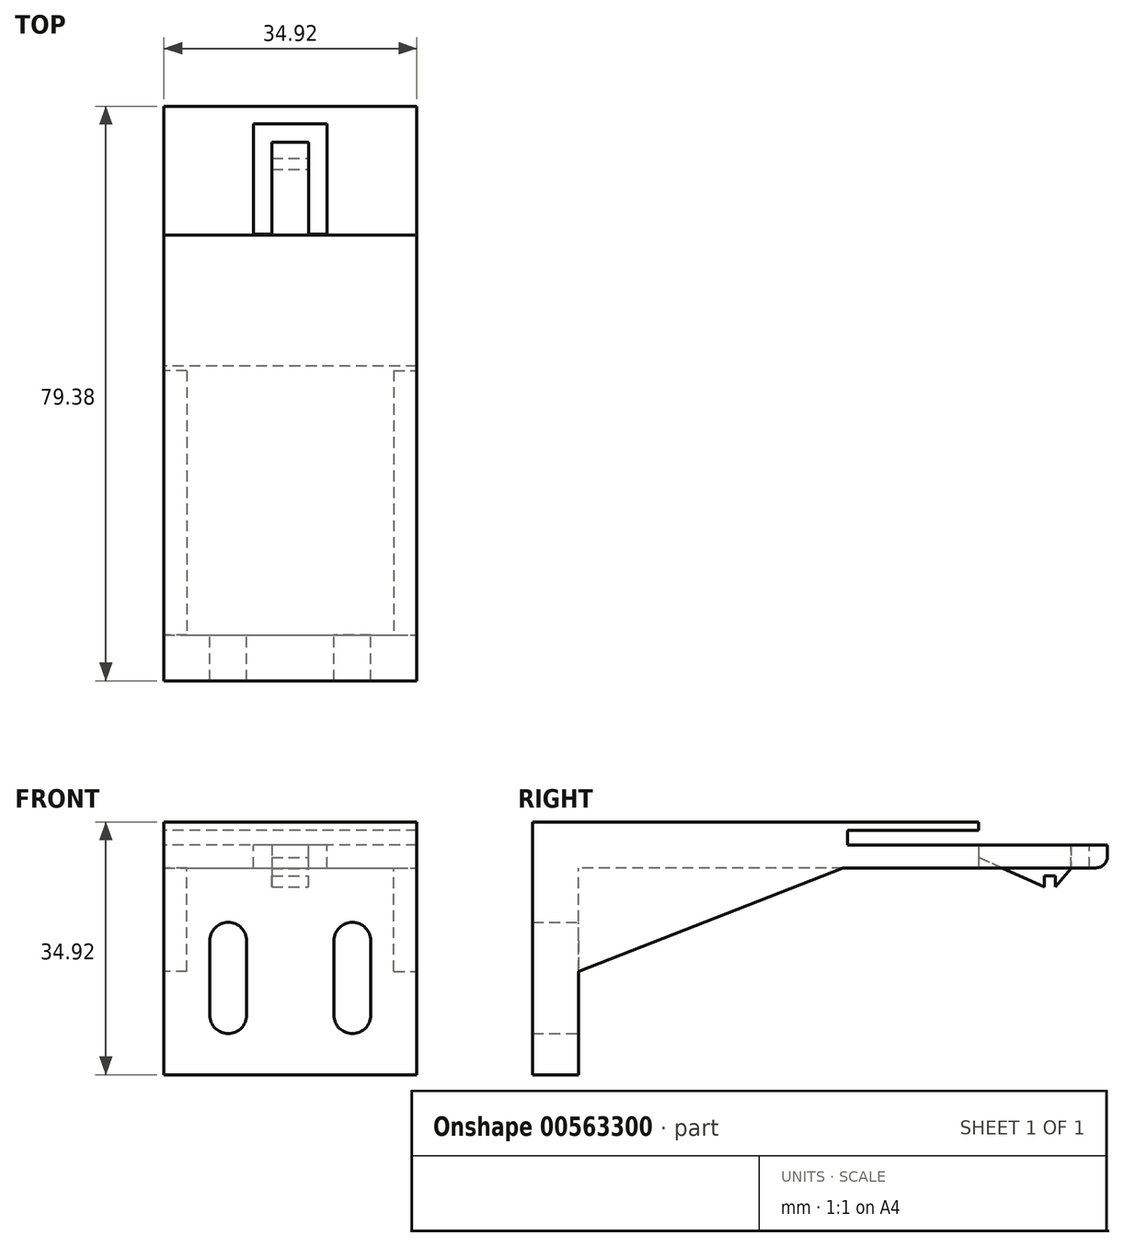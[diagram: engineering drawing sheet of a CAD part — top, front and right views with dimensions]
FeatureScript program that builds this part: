
annotation { "Feature Type Name" : "Feature", "Feature Type Description" : "" }
export const myFeature = defineFeature(function(context is Context, id is Id, definition is map)
    precondition{}
    {
        {
            var Q0;
            Q0=qCreatedBy(makeId("Front.planeOp"),FACE);
            var sketch = newSketch(context, id + "F0", { "sketchPlane" : qUnion([Q0])});
            skLineSegment(sketch, "E0.top", {"start": v(0, 34.93) * mm, "end": v(-34.93, 34.93) * mm});
            skLineSegment(sketch, "E0.left", {"start": v(0, 0) * mm, "end": v(0, 34.93) * mm});
            skLineSegment(sketch, "E0.right", {"start": v(-34.93, 0) * mm, "end": v(-34.93, 34.92) * mm});
            skLineSegment(sketch, "E1", {"start": v(-34.93, 0) * mm, "end": v(0, 0) * mm});
            skLineSegment(sketch, "E2", {"start": v(-28.57, 11.27) * mm, "end": v(-28.57, 5.29) * mm});
            skPoint(sketch, "E3.trimOffspring.end.orphan", {"position": v(-24.77, 14.54) * mm});
            skPoint(sketch, "E4.start.orphan", {"position": v(-24.77, 2.11) * mm});
            skLineSegment(sketch, "E5", {"start": v(-17.46, 0) * mm, "end": v(-17.46, 34.93) * mm});
            skLineSegment(sketch, "E6", {"start": v(-24.77, 14.54) * mm, "end": v(-24.77, 14.7) * mm});
            skArc(sketch, "E7", {"start": v(-6.35, 18.52) * mm, "mid": v(-8.9, 21.06) * mm, "end": v(-11.43, 18.52) * mm});
            skArc(sketch, "E8", {"start": v(-11.43, 8.21) * mm, "mid": v(-8.89, 5.67) * mm, "end": v(-6.35, 8.21) * mm});
            skLineSegment(sketch, "E9", {"start": v(-6.35, 18.52) * mm, "end": v(-6.35, 8.21) * mm});
            skLineSegment(sketch, "E10", {"start": v(-11.43, 18.52) * mm, "end": v(-11.43, 8.21) * mm});
            skPoint(sketch, "E11.start.orphan", {"position": v(-8.89, 2.11) * mm});
            skPoint(sketch, "E12.trimOffspring.end.orphan", {"position": v(-8.9, 34.93) * mm});
            skArc(sketch, "E13.MirrorCS", {"start": v(-23.5, 8.21) * mm, "mid": v(-26.04, 5.67) * mm, "end": v(-28.58, 8.21) * mm});
            skLineSegment(sketch, "E14.MirrorCS", {"start": v(-23.5, 18.52) * mm, "end": v(-23.5, 8.21) * mm});
            skLineSegment(sketch, "E15.MirrorCS", {"start": v(-28.58, 18.52) * mm, "end": v(-28.58, 8.21) * mm});
            skArc(sketch, "E16.MirrorCS", {"start": v(-28.58, 18.52) * mm, "mid": v(-26.04, 21.06) * mm, "end": v(-23.5, 18.52) * mm});
            skSolve(sketch);
        }
        {
            var Q0;
            Q0 = qSketchRegion(id + "F0", true);
            extrude(context, id + "F1", {"entities" : qUnion([Q0]), "depth" : 6.35 * mm, "offsetDistance" : 25.4 * mm});
        }
        {
            var Q0;
            Q0=makeQuery(id+"F1.opExtrude","CAP_FACE",FACE,{"disambiguationData":[OSD([sQuery(id+"F0.wireOp",EDGE,"E0.top"),sQuery(id+"F0.wireOp",EDGE,"E0.left"),sQuery(id+"F0.wireOp",EDGE,"E0.right"),sQuery(id+"F0.wireOp",EDGE,"E1"),sQuery(id+"F0.wireOp",EDGE,"E2"),sQuery(id+"F0.wireOp",EDGE,"H6N8bAam-MXU0-CgfR-VFbv-wHTDPL8jopEp"),sQuery(id+"F0.wireOp",EDGE,"061fb9ac-4066-484d-a823-505c24cabc42.trimOffspring"),sQuery(id+"F0.wireOp",EDGE,"351367ec-2027-426c-9255-262ef1abbde6.trimOffspring"),sQuery(id+"F0.wireOp",EDGE,"85143ae7-1432-489c-9ee5-68bd793780470.MirrorCS"),sQuery(id+"F0.wireOp",EDGE,"85143ae7-1432-489c-9ee5-68bd793780471.MirrorCS"),sQuery(id+"F0.wireOp",EDGE,"85143ae7-1432-489c-9ee5-68bd793780472.MirrorCS"),sQuery(id+"F0.wireOp",EDGE,"85143ae7-1432-489c-9ee5-68bd793780473.MirrorCS")])],"isStart":true});
            var sketch = newSketch(context, id + "F2", { "sketchPlane" : qUnion([Q0])});
            skLineSegment(sketch, "E17.bottom", {"start": v(34.93, 34.93) * mm, "end": v(0, 34.93) * mm});
            skLineSegment(sketch, "E17.top", {"start": v(34.93, 28.57) * mm, "end": v(0, 28.57) * mm});
            skLineSegment(sketch, "E17.left", {"start": v(34.93, 34.93) * mm, "end": v(34.93, 28.57) * mm});
            skLineSegment(sketch, "E17.right", {"start": v(0, 34.93) * mm, "end": v(0, 28.57) * mm});
            skSolve(sketch);
        }
        {
            var Q0;
            Q0=makeQuery(id+"F2.imprint","IMPRINT",FACE,{"disambiguationData":[TD([[makeQuery(id+"F2.imprint","IMPRINT",EDGE,{"derivedFrom":sQuery(id+"F2.wireOp",EDGE,"E17.bottom")}),-1.0]])]});
            extrude(context, id + "F3", {"entities" : qUnion([Q0]), "operationType" : NewBodyOperationType.ADD, "depth" : 73.02 * mm, "offsetDistance" : 25.4 * mm});
        }
        {
            var Q0;
            Q0=makeQuery(id+"F3.boolean.opBoolean","MERGE",FACE,{"derivedFrom":[makeQuery(id+"F1.opExtrude","SWEPT_FACE",FACE,{"disambiguationData":[OSD([sQuery(id+"F0.wireOp",EDGE,"E0.left")])]}),makeQuery(id+"F3.opExtrude","SWEPT_FACE",FACE,{"disambiguationData":[OSD([sQuery(id+"F2.wireOp",EDGE,"E17.right")])]})]});
            var sketch = newSketch(context, id + "F4", { "sketchPlane" : qUnion([Q0])});
            skLineSegment(sketch, "E18", {"start": v(0, 14.29) * mm, "end": v(36.51, 28.57) * mm});
            skLineSegment(sketch, "E19", {"start": v(36.51, 28.57) * mm, "end": v(0, 28.57) * mm});
            skLineSegment(sketch, "E20", {"start": v(0, 28.57) * mm, "end": v(0, 14.29) * mm});
            skSolve(sketch);
        }
        {
            var Q0;
            Q0=makeQuery(id+"F4.imprint","IMPRINT",FACE,{"disambiguationData":[TD([[makeQuery(id+"F4.imprint","IMPRINT",EDGE,{"derivedFrom":sQuery(id+"F4.wireOp",EDGE,"E18")}),1.0]])]});
            extrude(context, id + "F5", {"entities" : qUnion([Q0]), "operationType" : NewBodyOperationType.ADD, "oppositeDirection" : true, "depth" : 3.17 * mm, "offsetDistance" : 25.4 * mm});
        }
        {
            var Q0;
            Q0=makeQuery(id+"F3.boolean.opBoolean","MERGE",FACE,{"derivedFrom":[makeQuery(id+"F1.opExtrude","SWEPT_FACE",FACE,{"disambiguationData":[OSD([sQuery(id+"F0.wireOp",EDGE,"E0.right")])]}),makeQuery(id+"F3.opExtrude","SWEPT_FACE",FACE,{"disambiguationData":[OSD([sQuery(id+"F2.wireOp",EDGE,"E17.left")])]})]});
            var sketch = newSketch(context, id + "F6", { "sketchPlane" : qUnion([Q0])});
            skLineSegment(sketch, "E21", {"start": v(0, 14.29) * mm, "end": v(-36.51, 28.58) * mm});
            skLineSegment(sketch, "E22", {"start": v(-36.51, 28.58) * mm, "end": v(0, 28.58) * mm});
            skLineSegment(sketch, "E23", {"start": v(0, 28.58) * mm, "end": v(0, 14.29) * mm});
            skSolve(sketch);
        }
        {
            var Q0;
            Q0=makeQuery(id+"F6.imprint","IMPRINT",FACE,{"disambiguationData":[TD([[makeQuery(id+"F6.imprint","IMPRINT",EDGE,{"derivedFrom":sQuery(id+"F6.wireOp",EDGE,"E21")}),-1.0]])]});
            extrude(context, id + "F7", {"entities" : qUnion([Q0]), "operationType" : NewBodyOperationType.ADD, "oppositeDirection" : true, "depth" : 3.17 * mm, "offsetDistance" : 25.4 * mm});
        }
        {
            var Q0;
            Q0=makeQuery(id+"F3.opExtrude","CAP_FACE",FACE,{"disambiguationData":[OSD([sQuery(id+"F2.wireOp",EDGE,"E17.bottom"),sQuery(id+"F2.wireOp",EDGE,"E17.top"),sQuery(id+"F2.wireOp",EDGE,"E17.left"),sQuery(id+"F2.wireOp",EDGE,"E17.right")])],"isStart":false});
            var sketch = newSketch(context, id + "F8", { "sketchPlane" : qUnion([Q0])});
            skLineSegment(sketch, "E24", {"start": v(0, 31.75) * mm, "end": v(34.93, 31.75) * mm});
            skLineSegment(sketch, "E25.bottom", {"start": v(0, 34.93) * mm, "end": v(34.93, 34.93) * mm});
            skLineSegment(sketch, "E25.left", {"start": v(0, 34.93) * mm, "end": v(0, 31.75) * mm});
            skLineSegment(sketch, "E25.right", {"start": v(34.93, 34.93) * mm, "end": v(34.93, 31.75) * mm});
            skSolve(sketch);
        }
        {
            var Q0;
            Q0=makeQuery(id+"F8.imprint","IMPRINT",FACE,{"disambiguationData":[TD([[makeQuery(id+"F8.imprint","IMPRINT",EDGE,{"derivedFrom":sQuery(id+"F8.wireOp",EDGE,"E25.bottom")}),-1.0]])]});
            extrude(context, id + "F9", {"entities" : qUnion([Q0]), "operationType" : NewBodyOperationType.REMOVE, "oppositeDirection" : true, "depth" : 17.78 * mm, "offsetDistance" : 25.4 * mm});
        }
        {
            var Q0;
            Q0=makeQuery(id+"F9.boolean.opBoolean","COPY",FACE,{"derivedFrom":makeQuery(id+"F9.opExtrude","CAP_FACE",FACE,{"disambiguationData":[OSD([sQuery(id+"F8.wireOp",EDGE,"E25.bottom"),sQuery(id+"F8.wireOp",EDGE,"E24"),sQuery(id+"F8.wireOp",EDGE,"E25.left"),sQuery(id+"F8.wireOp",EDGE,"E25.right")])],"isStart":false})});
            var sketch = newSketch(context, id + "F10", { "sketchPlane" : qUnion([Q0])});
            skLineSegment(sketch, "E26.bottom", {"start": v(0, 32.64) * mm, "end": v(34.93, 32.64) * mm});
            skLineSegment(sketch, "E26.top", {"start": v(0, 33.78) * mm, "end": v(34.93, 33.78) * mm});
            skLineSegment(sketch, "E26.left", {"start": v(0, 32.64) * mm, "end": v(0, 33.78) * mm});
            skLineSegment(sketch, "E26.right", {"start": v(34.93, 32.64) * mm, "end": v(34.93, 33.78) * mm});
            skSolve(sketch);
        }
        {
            var Q0;
            Q0=makeQuery(id+"F10.imprint","IMPRINT",FACE,{"disambiguationData":[TD([[makeQuery(id+"F10.imprint","IMPRINT",EDGE,{"derivedFrom":sQuery(id+"F10.wireOp",EDGE,"E26.bottom")}),1.0]])]});
            var Q1;
            {var subQ0=sQuery(id+"F10.wireOp",EDGE,"E26.bottom");Q1=makeQuery(id+"F10.imprint","IMPRINT",FACE,{"disambiguationData":[TD([[makeQuery(id+"F10.imprint","IMPRINT",EDGE,{"derivedFrom":subQ0}),-1.0]])]});}
            extrude(context, id + "F11", {"entities" : qUnion([Q0, Q1]), "operationType" : NewBodyOperationType.REMOVE, "oppositeDirection" : true, "depth" : 18.1 * mm, "offsetDistance" : 25.4 * mm});
        }
        {
            var Q0;
            Q0=makeQuery(id+"F11.boolean.opBoolean","MERGE",FACE,{"derivedFrom":[makeQuery(id+"F9.boolean.opBoolean","COPY",FACE,{"derivedFrom":makeQuery(id+"F9.opExtrude","SWEPT_FACE",FACE,{"disambiguationData":[OSD([sQuery(id+"F8.wireOp",EDGE,"E24")])]})}),makeQuery(id+"F11.opExtrude","SWEPT_FACE",FACE,{"disambiguationData":[OSD([sQuery(id+"F10.wireOp",EDGE,"E26.bottom")])]})]});
            var sketch = newSketch(context, id + "F12", { "sketchPlane" : qUnion([Q0])});
            skLineSegment(sketch, "E27.bottom", {"start": v(-12.38, 70.56) * mm, "end": v(-22.54, 70.56) * mm});
            skLineSegment(sketch, "E27.top", {"start": v(-12.38, 55.32) * mm, "end": v(-22.54, 55.32) * mm});
            skLineSegment(sketch, "E27.left", {"start": v(-12.38, 70.56) * mm, "end": v(-12.38, 55.32) * mm});
            skLineSegment(sketch, "E27.right", {"start": v(-22.54, 70.56) * mm, "end": v(-22.54, 55.32) * mm});
            skPoint(sketch, "E27.middle", {"position": v(-17.46, 62.94) * mm});
            skSolve(sketch);
        }
        {
            var Q0;
            Q0=makeQuery(id+"F12.imprint","IMPRINT",FACE,{"disambiguationData":[TD([[makeQuery(id+"F12.imprint","IMPRINT",EDGE,{"derivedFrom":sQuery(id+"F12.wireOp",EDGE,"E27.bottom")}),1.0]])]});
            extrude(context, id + "F13", {"entities" : qUnion([Q0]), "operationType" : NewBodyOperationType.REMOVE, "oppositeDirection" : true, "depth" : 25.4 * mm, "offsetDistance" : 25.4 * mm});
        }
        {
            var Q0;
            Q0=makeQuery(id+"F13.boolean.opBoolean","COPY",FACE,{"derivedFrom":makeQuery(id+"F13.opExtrude","SWEPT_FACE",FACE,{"disambiguationData":[OSD([sQuery(id+"F12.wireOp",EDGE,"E27.top")])]})});
            var sketch = newSketch(context, id + "F14", { "sketchPlane" : qUnion([Q0])});
            skLineSegment(sketch, "E28.bottom", {"start": v(14.92, 30.16) * mm, "end": v(20, 30.16) * mm});
            skLineSegment(sketch, "E28.left", {"start": v(12.38, 30.16) * mm, "end": v(12.38, 30.16) * mm});
            skLineSegment(sketch, "E28.right", {"start": v(22.54, 30.16) * mm, "end": v(22.54, 30.16) * mm});
            skLineSegment(sketch, "E29.bottom", {"start": v(20, 25.97) * mm, "end": v(14.92, 25.97) * mm});
            skLineSegment(sketch, "E30", {"start": v(14.92, 30.16) * mm, "end": v(14.92, 25.97) * mm});
            skLineSegment(sketch, "E31", {"start": v(20, 30.16) * mm, "end": v(20, 25.97) * mm});
            skPoint(sketch, "E32.start.orphan", {"position": v(22.54, 25.97) * mm});
            skLineSegment(sketch, "E33", {"start": v(14.92, 30.16) * mm, "end": v(14.92, 30.96) * mm});
            skLineSegment(sketch, "E34", {"start": v(14.92, 30.96) * mm, "end": v(20, 30.96) * mm});
            skLineSegment(sketch, "E35", {"start": v(20, 30.96) * mm, "end": v(20, 30.16) * mm});
            skSolve(sketch);
        }
        {
            var Q0;
            Q0 = qSketchRegion(id + "F14", true);
            var Q1;
            {var subQ0=sQuery(id+"F14.wireOp",EDGE,"E28.top");Q1=makeQuery(id+"F14.imprint","IMPRINT",FACE,{"disambiguationData":[TD([[makeQuery(id+"F14.imprint","IMPRINT",EDGE,{"derivedFrom":subQ0}),-1.0]])]});}
            extrude(context, id + "F15", {"entities" : qUnion([Q0, Q1]), "operationType" : NewBodyOperationType.ADD, "depth" : 12.7 * mm, "offsetDistance" : 25.4 * mm});
        }
        {
            var Q0;
            Q0=makeQuery(id+"F15.opExtrude","SWEPT_FACE",FACE,{"disambiguationData":[OSD([sQuery(id+"F14.wireOp",EDGE,"E30")])]});
            var sketch = newSketch(context, id + "F16", { "sketchPlane" : qUnion([Q0])});
            skLineSegment(sketch, "E36", {"start": v(62.8, 25.97) * mm, "end": v(67.37, 25.97) * mm});
            skLineSegment(sketch, "E37", {"start": v(68.02, 25.97) * mm, "end": v(67.37, 25.97) * mm});
            skLineSegment(sketch, "E38", {"start": v(62.8, 25.97) * mm, "end": v(55.32, 25.97) * mm});
            skLineSegment(sketch, "E39", {"start": v(64.31, 25.97) * mm, "end": v(64.31, 27.5) * mm});
            skLineSegment(sketch, "E40", {"start": v(64.31, 27.5) * mm, "end": v(65.85, 27.5) * mm});
            skLineSegment(sketch, "E41", {"start": v(65.85, 27.5) * mm, "end": v(65.85, 25.97) * mm});
            skLineSegment(sketch, "E42", {"start": v(64.31, 25.97) * mm, "end": v(65.85, 25.97) * mm});
            skPoint(sketch, "E43.end.orphan", {"position": v(55.32, 29.99) * mm});
            skPoint(sketch, "E44.start.orphan", {"position": v(62.8, 27.5) * mm});
            skLineSegment(sketch, "E45", {"start": v(64.31, 25.97) * mm, "end": v(55.32, 29.99) * mm});
            skLineSegment(sketch, "E46", {"start": v(65.85, 25.97) * mm, "end": v(68.02, 28.46) * mm});
            skLineSegment(sketch, "E47", {"start": v(68.02, 28.46) * mm, "end": v(68.02, 25.97) * mm});
            skLineSegment(sketch, "E48", {"start": v(64.31, 25.97) * mm, "end": v(55.32, 25.97) * mm});
            skLineSegment(sketch, "E49", {"start": v(55.32, 29.99) * mm, "end": v(55.32, 25.97) * mm});
            skSolve(sketch);
        }
        {
            var Q0;
            Q0=makeQuery(id+"F16.imprint","IMPRINT",FACE,{"disambiguationData":[TD([[makeQuery(id+"F16.imprint","IMPRINT",EDGE,{"derivedFrom":sQuery(id+"F16.wireOp",EDGE,"E36")}),-1.0]])]});
            var Q1;
            {var subQ0=sQuery(id+"F16.wireOp",EDGE,"E45");Q1=makeQuery(id+"F16.imprint","IMPRINT",FACE,{"disambiguationData":[TD([[makeQuery(id+"F16.imprint","IMPRINT",EDGE,{"derivedFrom":subQ0}),1.0]])]});}
            extrude(context, id + "F17", {"entities" : qUnion([Q0, Q1]), "operationType" : NewBodyOperationType.REMOVE, "oppositeDirection" : true, "depth" : 5.74 * mm, "offsetDistance" : 25.4 * mm});
        }
        {
            var Q0;
            Q0=makeQuery(id+"F9.boolean.opBoolean","COPY",EDGE,{"derivedFrom":makeQuery(id+"F9.opExtrude","CAP_EDGE",EDGE,{"disambiguationData":[OSD([sQuery(id+"F8.wireOp",EDGE,"E24")])],"isStart":true})});
            var Q1;
            Q1=makeQuery(id+"F3.opExtrude","CAP_EDGE",EDGE,{"disambiguationData":[OSD([sQuery(id+"F2.wireOp",EDGE,"E17.top")])],"isStart":false});
            fillet(context, id + "F18", {"entities" : qUnion([Q0, Q1]), "radius" : 1.59 * mm, "tangentPropagation" : true, "allowEdgeOverflow" : false});
        }
        {
            var Q0;
            Q0=makeQuery(id+"F17.boolean.opBoolean","MERGE",FACE,{"derivedFrom":[makeQuery(id+"F13.boolean.opBoolean","COPY",FACE,{"derivedFrom":makeQuery(id+"F13.opExtrude","SWEPT_FACE",FACE,{"disambiguationData":[OSD([sQuery(id+"F12.wireOp",EDGE,"E27.top")])]})}),makeQuery(id+"F17.opExtrude","SWEPT_FACE",FACE,{"disambiguationData":[OSD([sQuery(id+"F16.wireOp",EDGE,"E49")])]})]});
            var sketch = newSketch(context, id + "F19", { "sketchPlane" : qUnion([Q0])});
            skLineSegment(sketch, "E50.bottom", {"start": v(14.92, 30.96) * mm, "end": v(20, 30.96) * mm});
            skLineSegment(sketch, "E50.top", {"start": v(14.92, 31.77) * mm, "end": v(20, 31.77) * mm});
            skLineSegment(sketch, "E50.left", {"start": v(14.92, 30.96) * mm, "end": v(14.92, 31.77) * mm});
            skLineSegment(sketch, "E50.right", {"start": v(20, 30.96) * mm, "end": v(20, 31.77) * mm});
            skSolve(sketch);
        }
        {
            var Q0;
            Q0=makeQuery(id+"F19.imprint","IMPRINT",FACE,{"disambiguationData":[TD([[makeQuery(id+"F19.imprint","IMPRINT",EDGE,{"derivedFrom":sQuery(id+"F19.wireOp",EDGE,"E50.bottom")}),1.0]])]});
            extrude(context, id + "F20", {"entities" : qUnion([Q0]), "operationType" : NewBodyOperationType.ADD, "depth" : 12.7 * mm, "offsetDistance" : 25.4 * mm});
        }
    });
